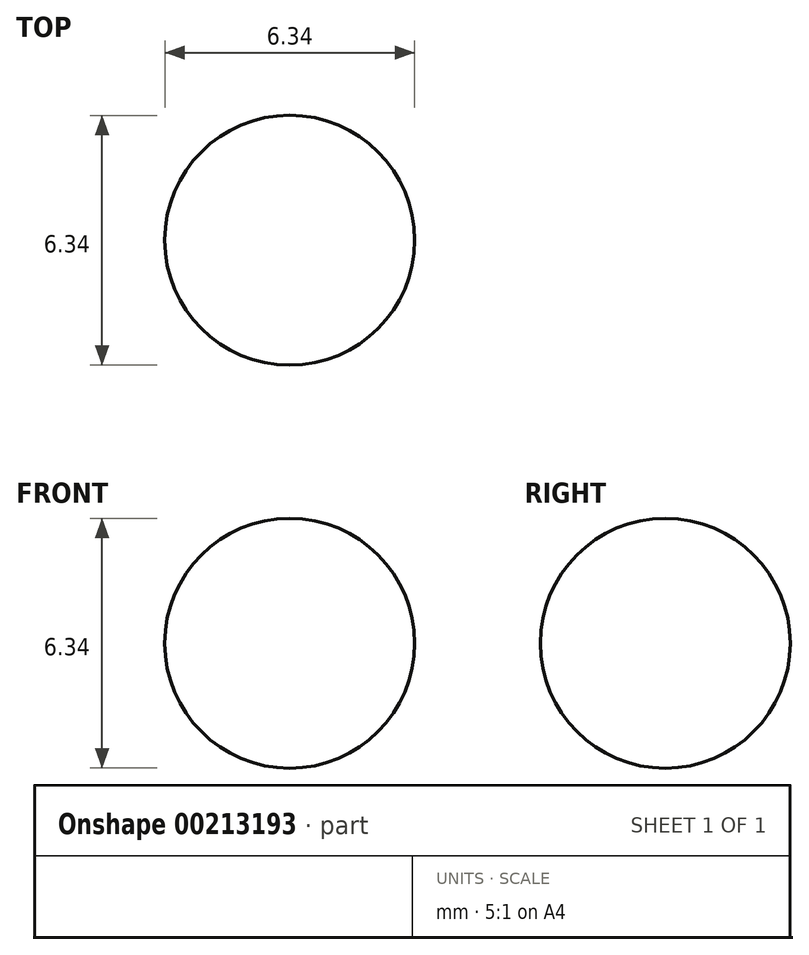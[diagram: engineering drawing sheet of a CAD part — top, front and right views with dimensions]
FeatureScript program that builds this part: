
annotation { "Feature Type Name" : "Feature", "Feature Type Description" : "" }
export const myFeature = defineFeature(function(context is Context, id is Id, definition is map)
    precondition{}
    {
        {
            var Q0;
            Q0=qCreatedBy(makeId("Front.planeOp"),FACE);
            var sketch = newSketch(context, id + "F0", { "sketchPlane" : qUnion([Q0])});
            skArc(sketch, "E0", {"start": v(0, -3.17) * mm, "mid": v(3.17, 0) * mm, "end": v(0, 3.17) * mm});
            skLineSegment(sketch, "E1", {"start": v(0, 3.17) * mm, "end": v(0, -3.17) * mm});
            skSolve(sketch);
        }
        {
            var Q0;
            Q0=makeQuery(id+"F0.imprint","IMPRINT",FACE,{"disambiguationData":[TD([[makeQuery(id+"F0.imprint","IMPRINT",EDGE,{"derivedFrom":sQuery(id+"F0.wireOp",EDGE,"E0")}),1.0]])]});
            var Q1;
            Q1=sQuery(id+"F0.wireOp",EDGE,"E1");
            revolve(context, id + "F1", {"entities" : qUnion([Q0]), "axis" : qUnion([Q1]), "revolveType" : RevolveType.FULL});
        }
    });
